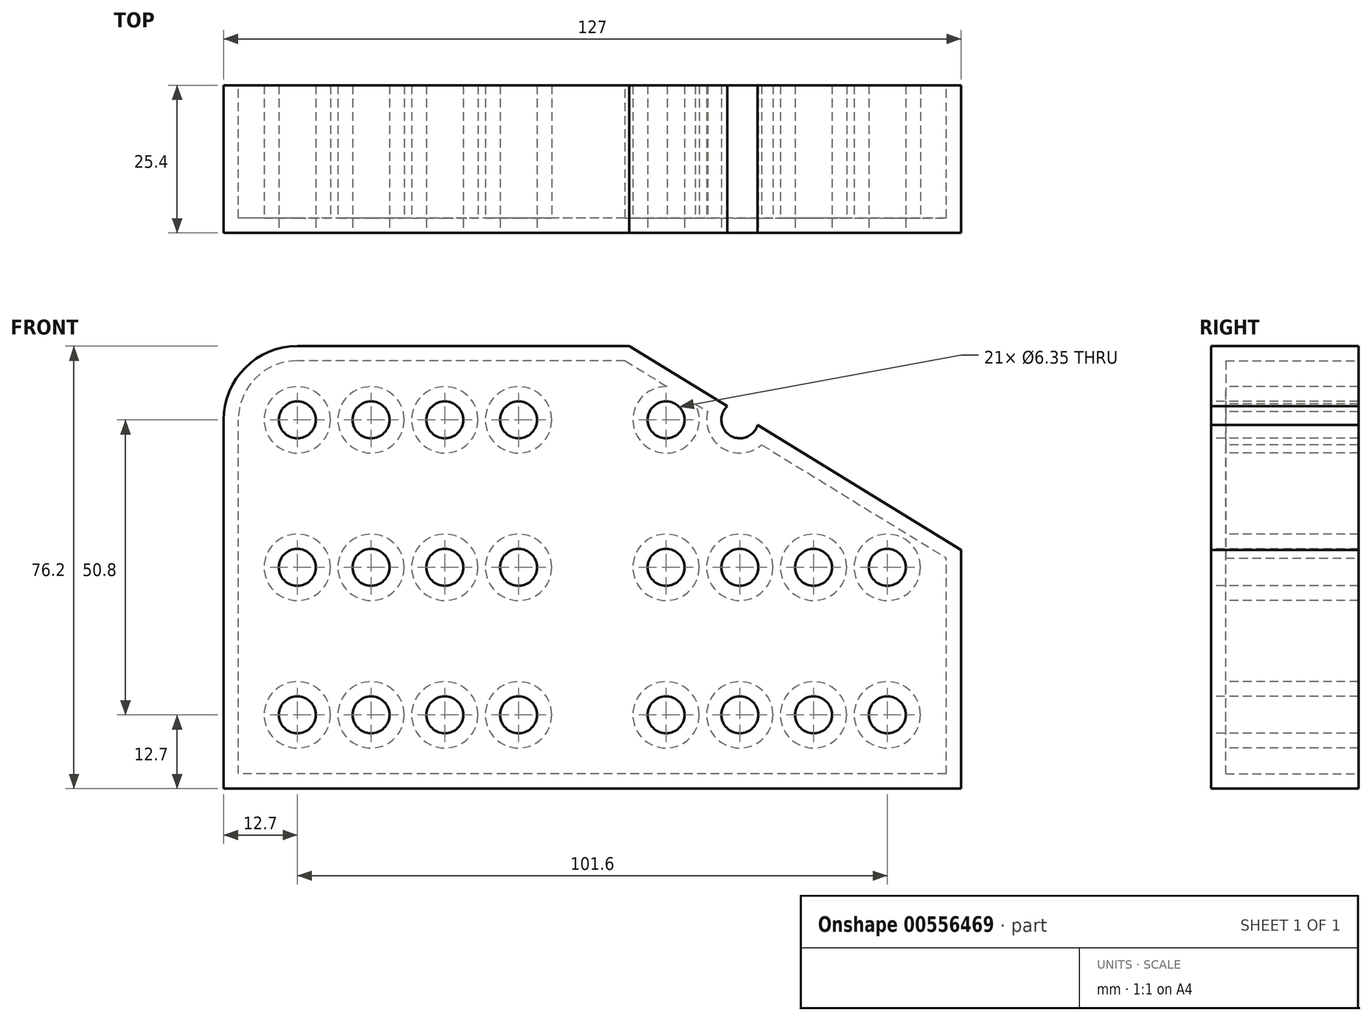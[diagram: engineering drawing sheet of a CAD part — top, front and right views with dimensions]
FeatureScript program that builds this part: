
annotation { "Feature Type Name" : "Feature", "Feature Type Description" : "" }
export const myFeature = defineFeature(function(context is Context, id is Id, definition is map)
    precondition{}
    {
        {
            var Q0;
            Q0=qCreatedBy(makeId("Front.planeOp"),FACE);
            var sketch = newSketch(context, id + "F0", { "sketchPlane" : qUnion([Q0])});
            skLineSegment(sketch, "E0.bottom", {"start": v(63.5, -38.1) * mm, "end": v(-63.5, -38.1) * mm});
            skLineSegment(sketch, "E0.top", {"start": v(6.35, 38.1) * mm, "end": v(-50.8, 38.1) * mm});
            skLineSegment(sketch, "E0.left", {"start": v(63.5, -38.1) * mm, "end": v(63.5, 3.02) * mm});
            skLineSegment(sketch, "E0.right", {"start": v(-63.5, -38.1) * mm, "end": v(-63.5, 25.4) * mm});
            skPoint(sketch, "E0.middle", {"position": v(0, 0) * mm});
            skPoint(sketch, "E1.visualSharp", {"position": v(-63.5, 38.1) * mm});
            skArc(sketch, "E1.filletArc", {"start": v(-50.8, 38.1) * mm, "mid": v(-59.78, 34.38) * mm, "end": v(-63.5, 25.4) * mm});
            skLineSegment(sketch, "E2", {"start": v(6.35, 38.1) * mm, "end": v(63.5, 3.02) * mm});
            skPoint(sketch, "E3.orphan", {"position": v(63.5, 38.1) * mm});
            skSolve(sketch);
        }
        {
            var Q0;
            Q0 = qSketchRegion(id + "F0", true);
            extrude(context, id + "F1", {"entities" : qUnion([Q0]), "depth" : 25.4 * mm, "offsetDistance" : 25.4 * mm});
        }
        {
            var Q0;
            Q0=makeQuery(id+"F1.opExtrude","CAP_FACE",FACE,{"disambiguationData":[OSD([sQuery(id+"F0.wireOp",EDGE,"E0.bottom"),sQuery(id+"F0.wireOp",EDGE,"E0.top"),sQuery(id+"F0.wireOp",EDGE,"E0.left"),sQuery(id+"F0.wireOp",EDGE,"E0.right"),sQuery(id+"F0.wireOp",EDGE,"E1.filletArc"),sQuery(id+"F0.wireOp",EDGE,"E2")])],"isStart":false});
            var sketch = newSketch(context, id + "F2", { "sketchPlane" : qUnion([Q0])});
            skCircle(sketch, "E4", {"center": v(-50.8, 25.4) * mm, "radius": 3.18 * mm});
            skCircle(sketch, "E5.0.1.0", {"center": v(-50.8, 0) * mm, "radius": 3.18 * mm});
            skCircle(sketch, "E5.0.2.0", {"center": v(-50.8, -25.4) * mm, "radius": 3.18 * mm});
            skCircle(sketch, "E5.1.0.0", {"center": v(-38.1, 25.4) * mm, "radius": 3.18 * mm});
            skCircle(sketch, "E5.1.1.0", {"center": v(-38.1, 0) * mm, "radius": 3.18 * mm});
            skCircle(sketch, "E5.1.2.0", {"center": v(-38.1, -25.4) * mm, "radius": 3.18 * mm});
            skCircle(sketch, "E5.2.0.0", {"center": v(-25.4, 25.4) * mm, "radius": 3.18 * mm});
            skCircle(sketch, "E5.2.1.0", {"center": v(-25.4, 0) * mm, "radius": 3.18 * mm});
            skCircle(sketch, "E5.2.2.0", {"center": v(-25.4, -25.4) * mm, "radius": 3.18 * mm});
            skCircle(sketch, "E5.3.0.0", {"center": v(-12.7, 25.4) * mm, "radius": 3.18 * mm});
            skCircle(sketch, "E5.3.1.0", {"center": v(-12.7, 0) * mm, "radius": 3.18 * mm});
            skCircle(sketch, "E5.3.2.0", {"center": v(-12.7, -25.4) * mm, "radius": 3.18 * mm});
            skLineSegment(sketch, "E5.direction1", {"start": v(-50.8, 25.4) * mm, "end": v(-38.1, 25.4) * mm, "construction": true});
            skLineSegment(sketch, "E5.direction2", {"start": v(-50.8, 25.4) * mm, "end": v(-50.8, 0) * mm, "construction": true});
            skLineSegment(sketch, "E6", {"start": v(0, 29.92) * mm, "end": v(0, -15.67) * mm, "construction": true});
            skCircle(sketch, "E7.MirrorC", {"center": v(25.4, 0) * mm, "radius": 3.18 * mm});
            skCircle(sketch, "E8.MirrorC", {"center": v(50.8, -25.4) * mm, "radius": 3.18 * mm});
            skCircle(sketch, "E9.MirrorC", {"center": v(38.1, -25.4) * mm, "radius": 3.18 * mm});
            skCircle(sketch, "E10.MirrorC", {"center": v(12.7, 0) * mm, "radius": 3.18 * mm});
            skCircle(sketch, "E11.MirrorC", {"center": v(50.8, 25.4) * mm, "radius": 3.18 * mm});
            skCircle(sketch, "E12.MirrorC", {"center": v(38.1, 25.4) * mm, "radius": 3.18 * mm});
            skCircle(sketch, "E13.MirrorC", {"center": v(25.4, 25.4) * mm, "radius": 3.18 * mm});
            skCircle(sketch, "E14.MirrorC", {"center": v(12.7, 25.4) * mm, "radius": 3.18 * mm});
            skCircle(sketch, "E15.MirrorC", {"center": v(38.1, 0) * mm, "radius": 3.18 * mm});
            skCircle(sketch, "E16.MirrorC", {"center": v(50.8, 0) * mm, "radius": 3.18 * mm});
            skCircle(sketch, "E17.MirrorC", {"center": v(25.4, -25.4) * mm, "radius": 3.18 * mm});
            skCircle(sketch, "E18.MirrorC", {"center": v(12.7, -25.4) * mm, "radius": 3.18 * mm});
            skSolve(sketch);
        }
        {
            var Q0;
            Q0 = qSketchRegion(id + "F2", true);
            extrude(context, id + "F3", {"entities" : qUnion([Q0]), "operationType" : NewBodyOperationType.REMOVE, "oppositeDirection" : true, "depth" : 25.4 * mm, "offsetDistance" : 25.4 * mm});
        }
        {
            var Q0;
            Q0=makeQuery(id+"F1.opExtrude","CAP_FACE",FACE,{"disambiguationData":[OSD([sQuery(id+"F0.wireOp",EDGE,"E0.bottom"),sQuery(id+"F0.wireOp",EDGE,"E0.top"),sQuery(id+"F0.wireOp",EDGE,"E0.left"),sQuery(id+"F0.wireOp",EDGE,"E0.right"),sQuery(id+"F0.wireOp",EDGE,"E1.filletArc"),sQuery(id+"F0.wireOp",EDGE,"E2")])],"isStart":true});
            shell(context, id + "F4", {"entities" : qUnion([Q0]), "thickness" : 2.54 * mm});
        }
    });
